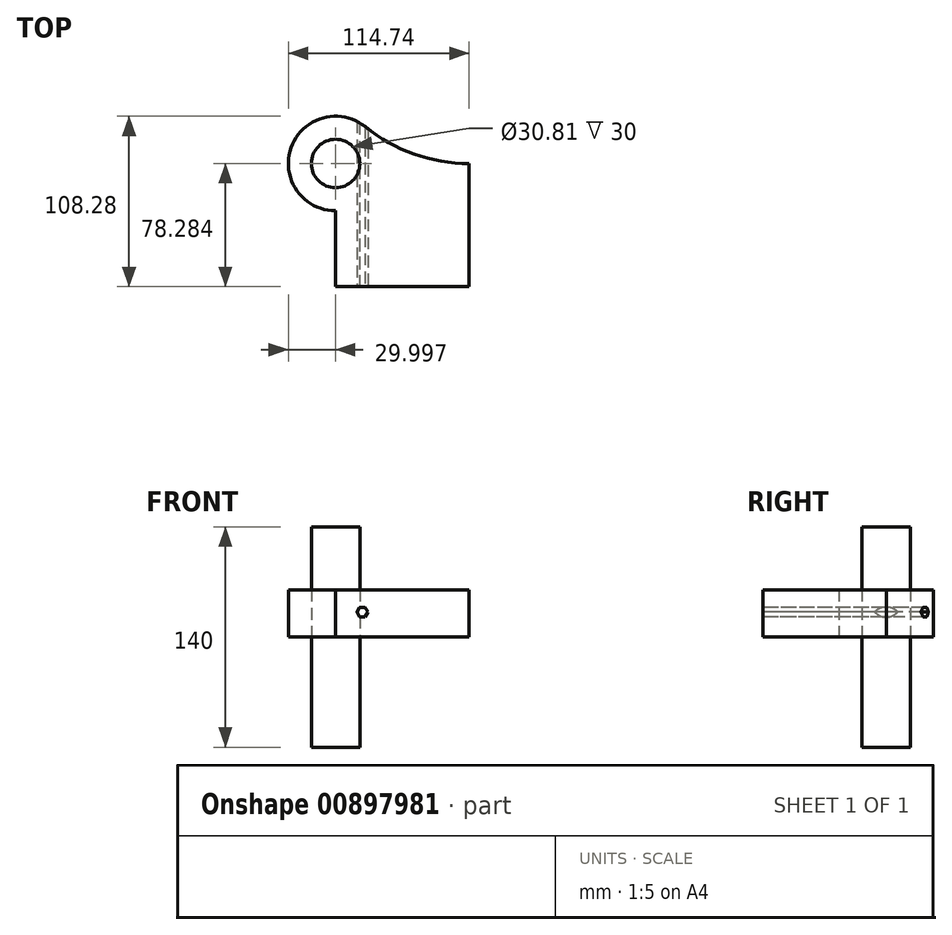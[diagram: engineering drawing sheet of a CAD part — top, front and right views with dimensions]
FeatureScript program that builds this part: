
annotation { "Feature Type Name" : "Feature", "Feature Type Description" : "" }
export const myFeature = defineFeature(function(context is Context, id is Id, definition is map)
    precondition{}
    {
        {
            var Q0;
            Q0=qCreatedBy(makeId("Top.planeOp"),FACE);
            var sketch = newSketch(context, id + "F0", { "sketchPlane" : qUnion([Q0])});
            skLineSegment(sketch, "E0.bottom", {"start": v(42.37, -39.14) * mm, "end": v(-42.37, -39.14) * mm});
            skLineSegment(sketch, "E0.top", {"start": v(42.37, 39.14) * mm, "end": v(-42.37, 39.14) * mm});
            skLineSegment(sketch, "E0.left", {"start": v(42.37, -39.14) * mm, "end": v(42.37, 39.14) * mm});
            skLineSegment(sketch, "E0.right", {"start": v(-42.37, -39.14) * mm, "end": v(-42.37, 39.14) * mm});
            skPoint(sketch, "E0.middle", {"position": v(0, 0) * mm});
            skCircle(sketch, "E1", {"center": v(-42.37, 39.14) * mm, "radius": 30 * mm});
            skArc(sketch, "E2", {"start": v(-23.5, 62.46) * mm, "mid": v(7.43, 45.15) * mm, "end": v(42.37, 39.14) * mm});
            skCircle(sketch, "E3", {"center": v(-42.37, 39.14) * mm, "radius": 15.4 * mm});
            skSolve(sketch);
        }
        {
            var Q0;
            {var subQ0=sQuery(id+"F0.wireOp",EDGE,"E1");var subQ2=sQuery(id+"F0.wireOp",EDGE,"E0.top");var subQ3=makeQuery(id+"F0.imprint","INTERSECT",VERTEX,{"derivedFrom":[subQ2,subQ0]});Q0=makeQuery(id+"F0.imprint","IMPRINT",FACE,{"disambiguationData":[TD([[makeQuery(id+"F0.imprint","IMPRINT",EDGE,{"disambiguationData":[TD([[subQ3,-1.0]])],"derivedFrom":subQ2}),-1.0]])]});}
            var Q1;
            {var subQ0=sQuery(id+"F0.wireOp",EDGE,"E2");Q1=makeQuery(id+"F0.imprint","IMPRINT",FACE,{"disambiguationData":[TD([[makeQuery(id+"F0.imprint","IMPRINT",EDGE,{"derivedFrom":subQ0}),-1.0]])]});}
            var Q2;
            {var subQ5=sQuery(id+"F0.wireOp",EDGE,"E0.bottom");Q2=makeQuery(id+"F0.imprint","IMPRINT",FACE,{"disambiguationData":[TD([[makeQuery(id+"F0.imprint","IMPRINT",EDGE,{"derivedFrom":subQ5}),-1.0]])]});}
            var Q3;
            {var subQ0=sQuery(id+"F0.wireOp",EDGE,"E1");var subQ1=sQuery(id+"F0.wireOp",EDGE,"E0.top");var subQ2=makeQuery(id+"F0.imprint","INTERSECT",VERTEX,{"derivedFrom":[subQ1,subQ0]});Q3=makeQuery(id+"F0.imprint","IMPRINT",FACE,{"disambiguationData":[TD([[makeQuery(id+"F0.imprint","IMPRINT",EDGE,{"disambiguationData":[TD([[subQ2,-1.0]])],"derivedFrom":subQ1}),1.0]])]});}
            extrude(context, id + "F1", {"entities" : qUnion([Q0, Q1, Q2, Q3]), "depth" : 30 * mm, "offsetDistance" : 25 * mm});
        }
        {
            var Q0;
            {var subQ0=sQuery(id+"F0.wireOp",EDGE,"E0.right");var subQ1=sQuery(id+"F0.wireOp",EDGE,"E0.top");var subQ2=makeQuery(id+"F0.imprint","INTERSECT",VERTEX,{"derivedFrom":[subQ1,subQ0]});Q0=makeQuery(id+"F0.imprint","IMPRINT",FACE,{"disambiguationData":[TD([[makeQuery(id+"F0.imprint","IMPRINT",EDGE,{"disambiguationData":[TD([[subQ2,1.0]])],"derivedFrom":subQ1}),-1.0]])]});}
            var Q1;
            {var subQ0=sQuery(id+"F0.wireOp",EDGE,"E0.right");var subQ1=sQuery(id+"F0.wireOp",EDGE,"E0.top");var subQ2=makeQuery(id+"F0.imprint","INTERSECT",VERTEX,{"derivedFrom":[subQ1,subQ0]});Q1=makeQuery(id+"F0.imprint","IMPRINT",FACE,{"disambiguationData":[TD([[makeQuery(id+"F0.imprint","IMPRINT",EDGE,{"disambiguationData":[TD([[subQ2,1.0]])],"derivedFrom":subQ1}),1.0]])]});}
            extrude(context, id + "F2", {"entities" : qUnion([Q0, Q1]), "depth" : 140 * mm, "offsetDistance" : 25 * mm, "symmetric" : true});
        }
        {
            var Q0;
            Q0=makeQuery(id+"F1.opExtrude","SWEPT_FACE",FACE,{"disambiguationData":[OSD([sQuery(id+"F0.wireOp",EDGE,"E0.bottom")])]});
            var sketch = newSketch(context, id + "F3", { "sketchPlane" : qUnion([Q0])});
            skCircle(sketch, "E4.cCircle", {"center": v(-25.37, 15.91) * mm, "radius": 3.01 * mm, "construction": true});
            skLineSegment(sketch, "E4.0", {"start": v(-21.9, 15.86) * mm, "end": v(-23.68, 12.87) * mm});
            skLineSegment(sketch, "E4.1", {"start": v(-23.68, 12.87) * mm, "end": v(-27.16, 12.93) * mm});
            skLineSegment(sketch, "E4.2", {"start": v(-27.16, 12.93) * mm, "end": v(-28.85, 15.96) * mm});
            skLineSegment(sketch, "E4.3", {"start": v(-28.85, 15.96) * mm, "end": v(-27.07, 18.95) * mm});
            skLineSegment(sketch, "E4.4", {"start": v(-27.07, 18.95) * mm, "end": v(-23.6, 18.9) * mm});
            skLineSegment(sketch, "E4.5", {"start": v(-23.6, 18.9) * mm, "end": v(-21.9, 15.86) * mm});
            skPoint(sketch, "E4.0.midPoint", {"position": v(-22.79, 14.37) * mm});
            skLineSegment(sketch, "E5.1.0.0", {"start": v(-12.4, 19.16) * mm, "end": v(-15.87, 19.21) * mm});
            skLineSegment(sketch, "E5.1.0.1", {"start": v(-17.56, 22.25) * mm, "end": v(-15.78, 25.24) * mm});
            skCircle(sketch, "E5.1.0.2", {"center": v(-14.09, 22.2) * mm, "radius": 3.01 * mm, "construction": true});
            skPoint(sketch, "E5.1.0.3", {"position": v(-11.5, 20.66) * mm});
            skLineSegment(sketch, "E5.1.0.4", {"start": v(-15.87, 19.21) * mm, "end": v(-17.56, 22.25) * mm});
            skLineSegment(sketch, "E5.1.0.5", {"start": v(-15.78, 25.24) * mm, "end": v(-12.3, 25.19) * mm});
            skLineSegment(sketch, "E5.1.0.6", {"start": v(-12.3, 25.19) * mm, "end": v(-10.6, 22.15) * mm});
            skLineSegment(sketch, "E5.1.0.7", {"start": v(-10.6, 22.15) * mm, "end": v(-12.4, 19.16) * mm});
            skLineSegment(sketch, "E5.direction1", {"start": v(-27.16, 12.93) * mm, "end": v(-15.87, 19.21) * mm, "construction": true});
            skSolve(sketch);
        }
        {
            var Q0;
            Q0=makeQuery(id+"F3.imprint","IMPRINT",FACE,{"disambiguationData":[TD([[makeQuery(id+"F3.imprint","IMPRINT",EDGE,{"derivedFrom":sQuery(id+"F3.wireOp",EDGE,"E4.0")}),-1.0]])]});
            extrude(context, id + "F4", {"entities" : qUnion([Q0]), "operationType" : NewBodyOperationType.REMOVE, "oppositeDirection" : true, "depth" : 125 * mm, "offsetDistance" : 25 * mm});
        }
    });
